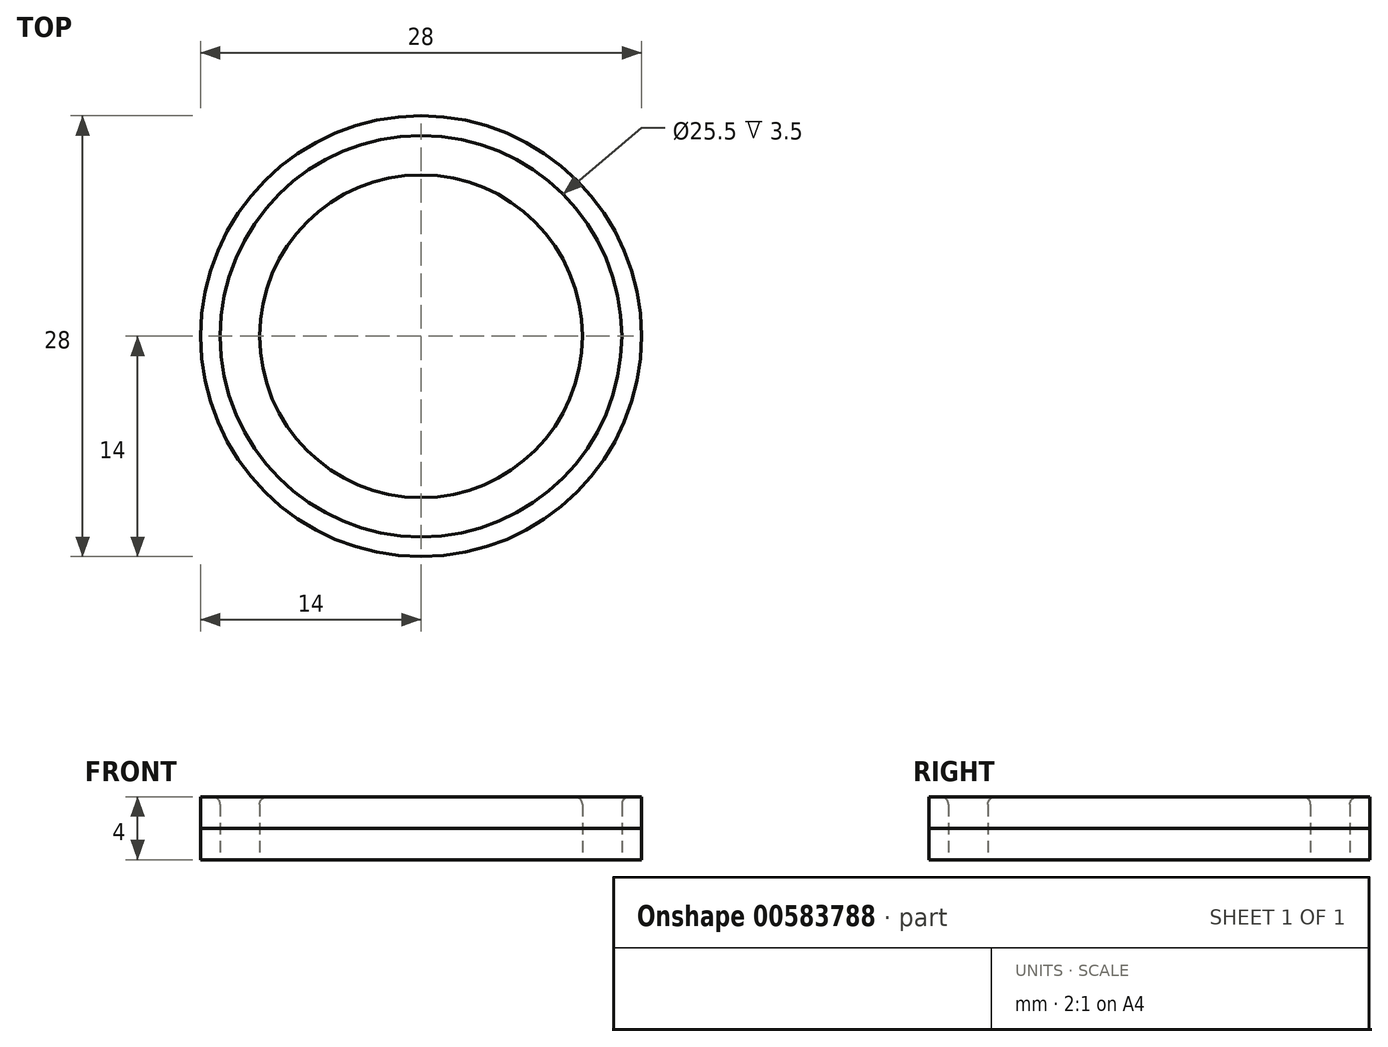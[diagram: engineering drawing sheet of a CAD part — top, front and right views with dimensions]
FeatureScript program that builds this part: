
annotation { "Feature Type Name" : "Feature", "Feature Type Description" : "" }
export const myFeature = defineFeature(function(context is Context, id is Id, definition is map)
    precondition{}
    {
        {
            var Q0;
            Q0=qCreatedBy(makeId("Top.planeOp"),FACE);
            var sketch = newSketch(context, id + "F0", { "sketchPlane" : qUnion([Q0])});
            skCircle(sketch, "E0", {"center": v(0, 0) * mm, "radius": 12.75 * mm});
            skCircle(sketch, "E1", {"center": v(0, 0) * mm, "radius": 14 * mm});
            skCircle(sketch, "E2", {"center": v(0, 0) * mm, "radius": 10.25 * mm});
            skSolve(sketch);
        }
        {
            var Q0;
            Q0=makeQuery(id+"F0.imprint","IMPRINT",FACE,{"disambiguationData":[TD([[makeQuery(id+"F0.imprint","IMPRINT",EDGE,{"derivedFrom":sQuery(id+"F0.wireOp",EDGE,"E0")}),-1.0]])]});
            var Q1;
            Q1=makeQuery(id+"F0.imprint","IMPRINT",FACE,{"disambiguationData":[TD([[makeQuery(id+"F0.imprint","IMPRINT",EDGE,{"derivedFrom":sQuery(id+"F0.wireOp",EDGE,"E2")}),1.0]])]});
            var Q2;
            Q2=makeQuery(id+"F0.imprint","IMPRINT",FACE,{"disambiguationData":[TD([[makeQuery(id+"F0.imprint","IMPRINT",EDGE,{"derivedFrom":sQuery(id+"F0.wireOp",EDGE,"E0")}),1.0]])]});
            extrude(context, id + "F1", {"entities" : qUnion([Q0, Q1, Q2]), "depth" : 2 * mm, "offsetDistance" : 25 * mm});
        }
        {
            var Q0;
            Q0=makeQuery(id+"F0.imprint","IMPRINT",FACE,{"disambiguationData":[TD([[makeQuery(id+"F0.imprint","IMPRINT",EDGE,{"derivedFrom":sQuery(id+"F0.wireOp",EDGE,"E0")}),-1.0]])]});
            var Q1;
            Q1=makeQuery(id+"F0.imprint","IMPRINT",FACE,{"disambiguationData":[TD([[makeQuery(id+"F0.imprint","IMPRINT",EDGE,{"derivedFrom":sQuery(id+"F0.wireOp",EDGE,"E2")}),1.0]])]});
            extrude(context, id + "F2", {"entities" : qUnion([Q0, Q1]), "depth" : 4 * mm, "offsetDistance" : 25 * mm});
        }
        {
            var Q0;
            Q0=makeQuery(id+"F2.opExtrude","CAP_EDGE",EDGE,{"disambiguationData":[OSD([sQuery(id+"F0.wireOp",EDGE,"E2")])],"isStart":false});
            fillet(context, id + "F3", {"entities" : qUnion([Q0]), "radius" : 0.5 * mm, "tangentPropagation" : true, "allowEdgeOverflow" : false});
        }
        {
            var Q0;
            Q0=makeQuery(id+"F2.opExtrude","CAP_EDGE",EDGE,{"disambiguationData":[OSD([sQuery(id+"F0.wireOp",EDGE,"E0")])],"isStart":false});
            fillet(context, id + "F4", {"entities" : qUnion([Q0]), "radius" : 0.5 * mm, "tangentPropagation" : true, "allowEdgeOverflow" : false});
        }
    });
